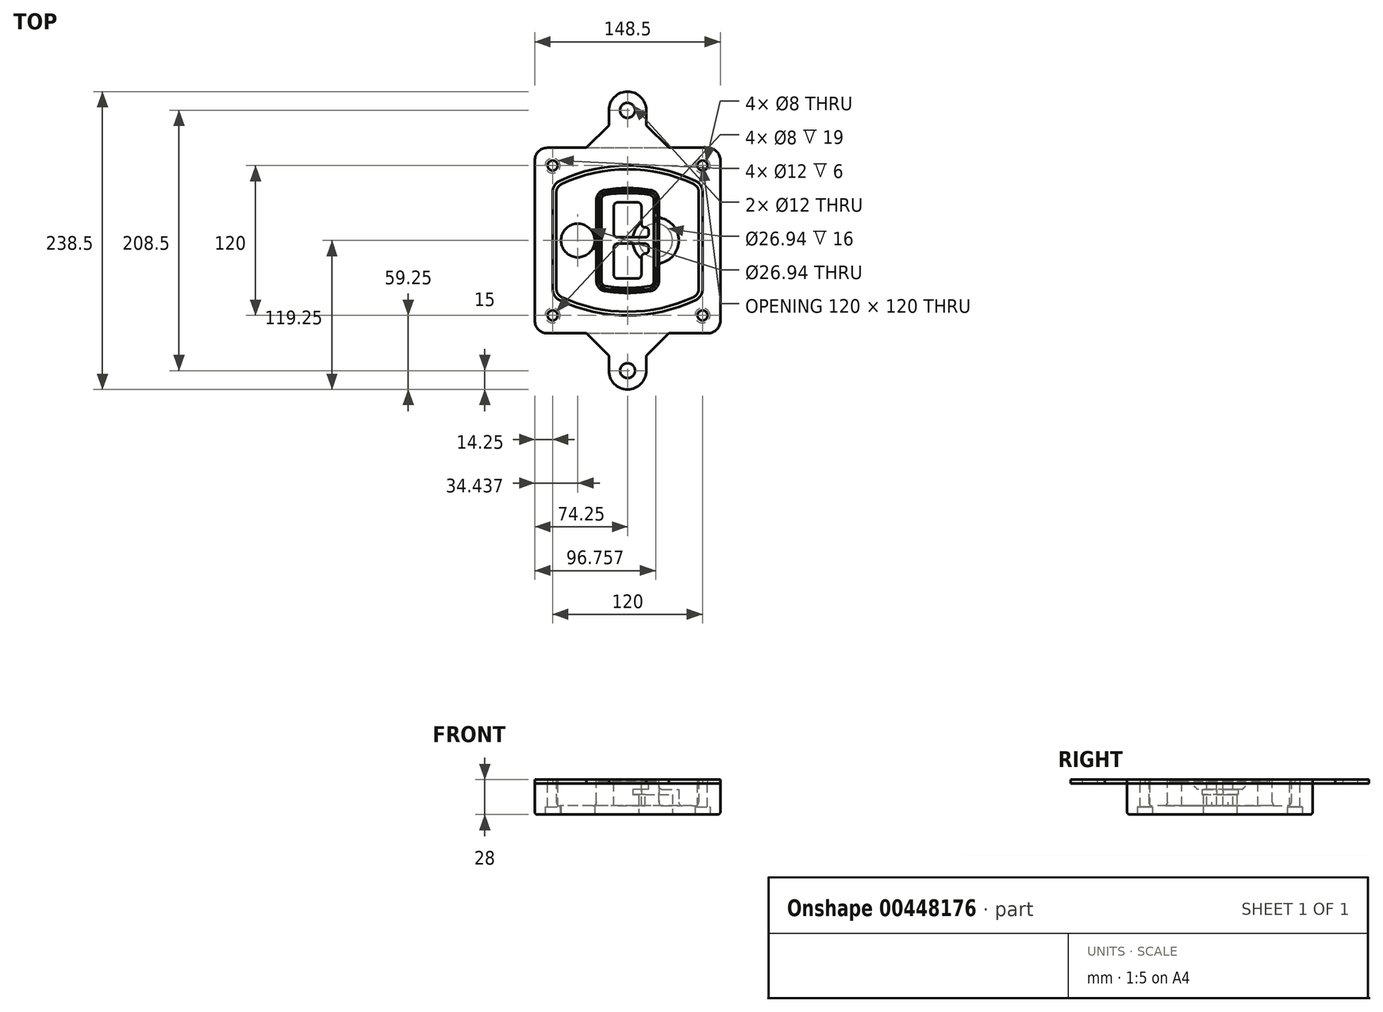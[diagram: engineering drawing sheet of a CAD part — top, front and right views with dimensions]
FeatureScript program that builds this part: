
annotation { "Feature Type Name" : "Feature", "Feature Type Description" : "" }
export const myFeature = defineFeature(function(context is Context, id is Id, definition is map)
    precondition{}
    {
        {
            var Q0;
            Q0=qCreatedBy(makeId("Top.planeOp"),FACE);
            var sketch = newSketch(context, id + "F0", { "sketchPlane" : qUnion([Q0])});
            skPoint(sketch, "E0.rect.middle", {"position": v(0, 0) * mm});
            skLineSegment(sketch, "E1.bottom", {"start": v(-64.25, -74.25) * mm, "end": v(64.25, -74.25) * mm});
            skLineSegment(sketch, "E1.top", {"start": v(-64.25, 74.25) * mm, "end": v(64.25, 74.25) * mm});
            skLineSegment(sketch, "E1.left", {"start": v(-74.25, -64.25) * mm, "end": v(-74.25, 64.25) * mm});
            skLineSegment(sketch, "E1.right", {"start": v(74.25, -64.25) * mm, "end": v(74.25, 64.25) * mm});
            skLineSegment(sketch, "E2", {"start": v(-74.25, 74.25) * mm, "end": v(74.25, -74.25) * mm, "construction": true});
            skLineSegment(sketch, "E3", {"start": v(74.25, 74.25) * mm, "end": v(-74.25, -74.25) * mm, "construction": true});
            skCircle(sketch, "E4", {"center": v(-60, 60) * mm, "radius": 4 * mm});
            skCircle(sketch, "E5", {"center": v(60, 60) * mm, "radius": 4 * mm});
            skCircle(sketch, "E6", {"center": v(60, -60) * mm, "radius": 4 * mm});
            skCircle(sketch, "E7", {"center": v(-60, -60) * mm, "radius": 4 * mm});
            skLineSegment(sketch, "E8", {"start": v(-60, 60) * mm, "end": v(60, 60) * mm, "construction": true});
            skLineSegment(sketch, "E9", {"start": v(60, 60) * mm, "end": v(60, -60) * mm, "construction": true});
            skLineSegment(sketch, "E10", {"start": v(60, -60) * mm, "end": v(-60, -60) * mm, "construction": true});
            skLineSegment(sketch, "E11", {"start": v(-60, -60) * mm, "end": v(-60, 60) * mm, "construction": true});
            skLineSegment(sketch, "E12", {"start": v(-60, 38.83) * mm, "end": v(-60, -38.83) * mm});
            skLineSegment(sketch, "E13", {"start": v(60, 38.83) * mm, "end": v(60, -38.83) * mm});
            skArc(sketch, "E14", {"start": v(54.26, 47.88) * mm, "mid": v(0, 60) * mm, "end": v(-54.26, 47.88) * mm});
            skArc(sketch, "E15", {"start": v(-54.26, -47.88) * mm, "mid": v(0, -60) * mm, "end": v(54.26, -47.88) * mm});
            skLineSegment(sketch, "E16", {"start": v(-60, 0) * mm, "end": v(60, 0) * mm, "construction": true});
            skPoint(sketch, "E17.visualSharp", {"position": v(-60, -45) * mm});
            skArc(sketch, "E17.filletArc", {"start": v(-60, -38.83) * mm, "mid": v(-58.44, -44.2) * mm, "end": v(-54.26, -47.88) * mm});
            skPoint(sketch, "E18.visualSharp", {"position": v(-60, 45) * mm});
            skArc(sketch, "E18.filletArc", {"start": v(-54.26, 47.88) * mm, "mid": v(-58.44, 44.2) * mm, "end": v(-60, 38.83) * mm});
            skPoint(sketch, "E19.visualSharp", {"position": v(60, 45) * mm});
            skArc(sketch, "E19.filletArc", {"start": v(60, 38.83) * mm, "mid": v(58.44, 44.2) * mm, "end": v(54.26, 47.88) * mm});
            skPoint(sketch, "E20.visualSharp", {"position": v(60, -45) * mm});
            skArc(sketch, "E20.filletArc", {"start": v(54.26, -47.88) * mm, "mid": v(58.44, -44.2) * mm, "end": v(60, -38.83) * mm});
            skPoint(sketch, "E21.visualSharp", {"position": v(-74.25, 74.25) * mm});
            skArc(sketch, "E21.filletArc", {"start": v(-64.25, 74.25) * mm, "mid": v(-71.32, 71.32) * mm, "end": v(-74.25, 64.25) * mm});
            skPoint(sketch, "E22.visualSharp", {"position": v(74.25, 74.25) * mm});
            skArc(sketch, "E22.filletArc", {"start": v(74.25, 64.25) * mm, "mid": v(71.32, 71.32) * mm, "end": v(64.25, 74.25) * mm});
            skPoint(sketch, "E23.visualSharp", {"position": v(74.25, -74.25) * mm});
            skArc(sketch, "E23.filletArc", {"start": v(64.25, -74.25) * mm, "mid": v(71.32, -71.32) * mm, "end": v(74.25, -64.25) * mm});
            skPoint(sketch, "E24.visualSharp", {"position": v(-74.25, -74.25) * mm});
            skArc(sketch, "E24.filletArc", {"start": v(-74.25, -64.25) * mm, "mid": v(-71.32, -71.32) * mm, "end": v(-64.25, -74.25) * mm});
            skArc(sketch, "E25.0", {"start": v(57, 38.83) * mm, "mid": v(55.9, 42.58) * mm, "end": v(52.98, 45.17) * mm});
            skLineSegment(sketch, "E25.1", {"start": v(57, 38.83) * mm, "end": v(57, -38.83) * mm});
            skArc(sketch, "E25.2", {"start": v(52.98, -45.17) * mm, "mid": v(55.9, -42.58) * mm, "end": v(57, -38.83) * mm});
            skArc(sketch, "E25.3", {"start": v(-52.98, -45.17) * mm, "mid": v(0, -57) * mm, "end": v(52.98, -45.17) * mm});
            skArc(sketch, "E25.4", {"start": v(-57, -38.83) * mm, "mid": v(-55.9, -42.58) * mm, "end": v(-52.98, -45.17) * mm});
            skArc(sketch, "E25.5", {"start": v(52.98, 45.17) * mm, "mid": v(0, 57) * mm, "end": v(-52.98, 45.17) * mm});
            skLineSegment(sketch, "E25.6", {"start": v(-57, 38.83) * mm, "end": v(-57, -38.83) * mm});
            skArc(sketch, "E25.7", {"start": v(-52.98, 45.17) * mm, "mid": v(-55.9, 42.58) * mm, "end": v(-57, 38.83) * mm});
            skArc(sketch, "E26.0", {"start": v(-55.96, 51.5) * mm, "mid": v(-61.82, 46.33) * mm, "end": v(-64, 38.83) * mm});
            skArc(sketch, "E26.1", {"start": v(55.96, 51.5) * mm, "mid": v(0, 64) * mm, "end": v(-55.96, 51.5) * mm});
            skArc(sketch, "E26.2", {"start": v(64, 38.83) * mm, "mid": v(61.82, 46.33) * mm, "end": v(55.96, 51.5) * mm});
            skLineSegment(sketch, "E26.3", {"start": v(64, 38.83) * mm, "end": v(64, -38.83) * mm});
            skArc(sketch, "E26.4", {"start": v(55.96, -51.5) * mm, "mid": v(61.82, -46.33) * mm, "end": v(64, -38.83) * mm});
            skLineSegment(sketch, "E26.5", {"start": v(-64, 38.83) * mm, "end": v(-64, -38.83) * mm});
            skArc(sketch, "E26.6", {"start": v(-55.96, -51.5) * mm, "mid": v(0, -64) * mm, "end": v(55.96, -51.5) * mm});
            skArc(sketch, "E26.7", {"start": v(-64, -38.83) * mm, "mid": v(-61.82, -46.33) * mm, "end": v(-55.96, -51.5) * mm});
            skSolve(sketch);
        }
        {
            var Q0;
            Q0=makeQuery(id+"F0.imprint","IMPRINT",FACE,{"disambiguationData":[TD([[makeQuery(id+"F0.imprint","IMPRINT",EDGE,{"derivedFrom":sQuery(id+"F0.wireOp",EDGE,"E1.bottom")}),1.0]])]});
            var Q1;
            Q1=makeQuery(id+"F0.imprint","IMPRINT",FACE,{"disambiguationData":[TD([[makeQuery(id+"F0.imprint","IMPRINT",EDGE,{"derivedFrom":sQuery(id+"F0.wireOp",EDGE,"E12")}),1.0]])]});
            var Q2;
            Q2=makeQuery(id+"F0.imprint","IMPRINT",FACE,{"disambiguationData":[TD([[makeQuery(id+"F0.imprint","IMPRINT",EDGE,{"derivedFrom":sQuery(id+"F0.wireOp",EDGE,"E25.0")}),1.0]])]});
            var Q3;
            Q3=makeQuery(id+"F0.imprint","IMPRINT",FACE,{"disambiguationData":[TD([[makeQuery(id+"F0.imprint","IMPRINT",EDGE,{"derivedFrom":sQuery(id+"F0.wireOp",EDGE,"E12")}),-1.0]])]});
            extrude(context, id + "F1", {"entities" : qUnion([Q0, Q1, Q2, Q3]), "oppositeDirection" : true, "depth" : 25 * mm});
        }
        {
            var Q0;
            Q0=makeQuery(id+"F0.imprint","IMPRINT",FACE,{"disambiguationData":[TD([[makeQuery(id+"F0.imprint","IMPRINT",EDGE,{"derivedFrom":sQuery(id+"F0.wireOp",EDGE,"E12")}),1.0]])]});
            extrude(context, id + "F2", {"entities" : qUnion([Q0]), "operationType" : NewBodyOperationType.ADD, "depth" : 3 * mm});
        }
        {
            var Q0;
            Q0=makeQuery(id+"F0.imprint","IMPRINT",FACE,{"disambiguationData":[TD([[makeQuery(id+"F0.imprint","IMPRINT",EDGE,{"derivedFrom":sQuery(id+"F0.wireOp",EDGE,"E25.0")}),1.0]])]});
            extrude(context, id + "F3", {"entities" : qUnion([Q0]), "operationType" : NewBodyOperationType.REMOVE, "oppositeDirection" : true, "depth" : 18 * mm});
        }
        {
            var Q0;
            Q0=makeQuery(id+"F2.opExtrude","CAP_FACE",FACE,{"disambiguationData":[OSD([sQuery(id+"F0.wireOp",EDGE,"E12"),sQuery(id+"F0.wireOp",EDGE,"E13"),sQuery(id+"F0.wireOp",EDGE,"E14"),sQuery(id+"F0.wireOp",EDGE,"E15"),sQuery(id+"F0.wireOp",EDGE,"E17.filletArc"),sQuery(id+"F0.wireOp",EDGE,"E18.filletArc"),sQuery(id+"F0.wireOp",EDGE,"E19.filletArc"),sQuery(id+"F0.wireOp",EDGE,"E20.filletArc"),sQuery(id+"F0.wireOp",EDGE,"E25.0"),sQuery(id+"F0.wireOp",EDGE,"E25.1"),sQuery(id+"F0.wireOp",EDGE,"E25.2"),sQuery(id+"F0.wireOp",EDGE,"E25.3"),sQuery(id+"F0.wireOp",EDGE,"E25.4"),sQuery(id+"F0.wireOp",EDGE,"E25.5"),sQuery(id+"F0.wireOp",EDGE,"E25.6"),sQuery(id+"F0.wireOp",EDGE,"E25.7")])],"isStart":false});
            var sketch = newSketch(context, id + "F4", { "sketchPlane" : qUnion([Q0])});
            skArc(sketch, "E27.0", {"start": v(-18.34, -40.45) * mm, "mid": v(0, -42) * mm, "end": v(18.34, -40.45) * mm});
            skArc(sketch, "E28.0", {"start": v(18.34, 40.45) * mm, "mid": v(0, 42) * mm, "end": v(-18.34, 40.45) * mm});
            skLineSegment(sketch, "E29", {"start": v(-25, 32.57) * mm, "end": v(-25, -32.57) * mm});
            skLineSegment(sketch, "E30", {"start": v(25, 32.57) * mm, "end": v(25, -32.57) * mm});
            skLineSegment(sketch, "E31", {"start": v(-25, 39.1) * mm, "end": v(25, 39.1) * mm, "construction": true});
            skLineSegment(sketch, "E32", {"start": v(-25, -39.1) * mm, "end": v(25, -39.1) * mm, "construction": true});
            skPoint(sketch, "E33.visualSharp", {"position": v(-25, 39.1) * mm});
            skArc(sketch, "E33.filletArc", {"start": v(-18.34, 40.45) * mm, "mid": v(-23.11, 37.73) * mm, "end": v(-25, 32.57) * mm});
            skPoint(sketch, "E34.visualSharp", {"position": v(25, 39.1) * mm});
            skArc(sketch, "E34.filletArc", {"start": v(25, 32.57) * mm, "mid": v(23.11, 37.73) * mm, "end": v(18.34, 40.45) * mm});
            skPoint(sketch, "E35.visualSharp", {"position": v(25, -39.1) * mm});
            skArc(sketch, "E35.filletArc", {"start": v(18.34, -40.45) * mm, "mid": v(23.11, -37.73) * mm, "end": v(25, -32.57) * mm});
            skPoint(sketch, "E36.visualSharp", {"position": v(-25, -39.1) * mm});
            skArc(sketch, "E36.filletArc", {"start": v(-25, -32.57) * mm, "mid": v(-23.11, -37.73) * mm, "end": v(-18.34, -40.45) * mm});
            skArc(sketch, "E37.0", {"start": v(52.98, 45.17) * mm, "mid": v(0, 57) * mm, "end": v(-52.98, 45.17) * mm});
            skArc(sketch, "E37.1", {"start": v(-52.98, 45.17) * mm, "mid": v(-55.9, 42.58) * mm, "end": v(-57, 38.83) * mm});
            skLineSegment(sketch, "E37.2", {"start": v(-57, 38.83) * mm, "end": v(-57, -38.83) * mm});
            skArc(sketch, "E37.3", {"start": v(-57, -38.83) * mm, "mid": v(-55.9, -42.58) * mm, "end": v(-52.98, -45.17) * mm});
            skArc(sketch, "E37.4", {"start": v(-52.98, -45.17) * mm, "mid": v(0, -57) * mm, "end": v(52.98, -45.17) * mm});
            skArc(sketch, "E37.5", {"start": v(52.98, -45.17) * mm, "mid": v(55.9, -42.58) * mm, "end": v(57, -38.83) * mm});
            skLineSegment(sketch, "E37.6", {"start": v(57, 38.83) * mm, "end": v(57, -38.83) * mm});
            skArc(sketch, "E37.7", {"start": v(57, 38.83) * mm, "mid": v(55.9, 42.58) * mm, "end": v(52.98, 45.17) * mm});
            skLineSegment(sketch, "E38.0", {"start": v(23, 32.57) * mm, "end": v(23, -32.57) * mm});
            skArc(sketch, "E38.1", {"start": v(18, -38.48) * mm, "mid": v(21.58, -36.44) * mm, "end": v(23, -32.57) * mm});
            skArc(sketch, "E38.2", {"start": v(-18, -38.48) * mm, "mid": v(0, -40) * mm, "end": v(18, -38.48) * mm});
            skArc(sketch, "E38.3", {"start": v(-23, -32.57) * mm, "mid": v(-21.58, -36.44) * mm, "end": v(-18, -38.48) * mm});
            skLineSegment(sketch, "E38.4", {"start": v(-23, 32.57) * mm, "end": v(-23, -32.57) * mm});
            skArc(sketch, "E38.5", {"start": v(23, 32.57) * mm, "mid": v(21.58, 36.44) * mm, "end": v(18, 38.48) * mm});
            skArc(sketch, "E38.6", {"start": v(-18, 38.48) * mm, "mid": v(-21.58, 36.44) * mm, "end": v(-23, 32.57) * mm});
            skArc(sketch, "E38.7", {"start": v(18, 38.48) * mm, "mid": v(0, 40) * mm, "end": v(-18, 38.48) * mm});
            skArc(sketch, "E39.0", {"start": v(21, 32.57) * mm, "mid": v(20.06, 35.15) * mm, "end": v(17.67, 36.5) * mm});
            skLineSegment(sketch, "E39.1", {"start": v(21, 32.57) * mm, "end": v(21, -32.57) * mm});
            skArc(sketch, "E39.2", {"start": v(17.67, -36.5) * mm, "mid": v(20.06, -35.15) * mm, "end": v(21, -32.57) * mm});
            skArc(sketch, "E39.3", {"start": v(-17.67, -36.5) * mm, "mid": v(0, -38) * mm, "end": v(17.67, -36.5) * mm});
            skArc(sketch, "E39.4", {"start": v(-21, -32.57) * mm, "mid": v(-20.06, -35.15) * mm, "end": v(-17.67, -36.5) * mm});
            skArc(sketch, "E39.5", {"start": v(17.67, 36.5) * mm, "mid": v(0, 38) * mm, "end": v(-17.67, 36.5) * mm});
            skLineSegment(sketch, "E39.6", {"start": v(-21, 32.57) * mm, "end": v(-21, -32.57) * mm});
            skArc(sketch, "E39.7", {"start": v(-17.67, 36.5) * mm, "mid": v(-20.06, 35.15) * mm, "end": v(-21, 32.57) * mm});
            skLineSegment(sketch, "E40", {"start": v(-25, 0) * mm, "end": v(25, 0) * mm, "construction": true});
            skLineSegment(sketch, "E41", {"start": v(-11, 5.5) * mm, "end": v(-11, 27.5) * mm});
            skLineSegment(sketch, "E42", {"start": v(-8, 30.5) * mm, "end": v(8, 30.5) * mm});
            skLineSegment(sketch, "E43", {"start": v(11, 27.5) * mm, "end": v(11, 13.5) * mm});
            skLineSegment(sketch, "E44", {"start": v(14, 10.5) * mm, "end": v(14, 10.5) * mm});
            skLineSegment(sketch, "E45", {"start": v(17, 7.5) * mm, "end": v(17, 5.5) * mm});
            skLineSegment(sketch, "E46", {"start": v(14, 2.5) * mm, "end": v(-8, 2.5) * mm});
            skPoint(sketch, "E47.visualSharp", {"position": v(-11, 30.5) * mm});
            skArc(sketch, "E47.filletArc", {"start": v(-8, 30.5) * mm, "mid": v(-10.12, 29.62) * mm, "end": v(-11, 27.5) * mm});
            skPoint(sketch, "E48.visualSharp", {"position": v(11, 30.5) * mm});
            skArc(sketch, "E48.filletArc", {"start": v(11, 27.5) * mm, "mid": v(10.12, 29.62) * mm, "end": v(8, 30.5) * mm});
            skPoint(sketch, "E49.visualSharp", {"position": v(11, 10.5) * mm});
            skArc(sketch, "E49.filletArc", {"start": v(11, 13.5) * mm, "mid": v(11.88, 11.38) * mm, "end": v(14, 10.5) * mm});
            skPoint(sketch, "E50.visualSharp", {"position": v(17, 10.5) * mm});
            skArc(sketch, "E50.filletArc", {"start": v(17, 7.5) * mm, "mid": v(16.12, 9.62) * mm, "end": v(14, 10.5) * mm});
            skPoint(sketch, "E51.visualSharp", {"position": v(17, 2.5) * mm});
            skArc(sketch, "E51.filletArc", {"start": v(14, 2.5) * mm, "mid": v(16.12, 3.38) * mm, "end": v(17, 5.5) * mm});
            skPoint(sketch, "E52.visualSharp", {"position": v(-11, 2.5) * mm});
            skArc(sketch, "E52.filletArc", {"start": v(-11, 5.5) * mm, "mid": v(-10.12, 3.38) * mm, "end": v(-8, 2.5) * mm});
            skLineSegment(sketch, "E53.0.MirrorCS", {"start": v(14, -2.5) * mm, "end": v(-8, -2.5) * mm});
            skArc(sketch, "E54.0.MirrorCS", {"start": v(-11, -5.5) * mm, "mid": v(-10.12, -3.38) * mm, "end": v(-8, -2.5) * mm});
            skLineSegment(sketch, "E55.0.MirrorCS", {"start": v(-11, -5.5) * mm, "end": v(-11, -27.5) * mm});
            skArc(sketch, "E56.0.MirrorCS", {"start": v(-8, -30.5) * mm, "mid": v(-10.12, -29.62) * mm, "end": v(-11, -27.5) * mm});
            skLineSegment(sketch, "E57.0.MirrorCS", {"start": v(-8, -30.5) * mm, "end": v(8, -30.5) * mm});
            skArc(sketch, "E58.0.MirrorCS", {"start": v(11, -27.5) * mm, "mid": v(10.12, -29.62) * mm, "end": v(8, -30.5) * mm});
            skLineSegment(sketch, "E59.0.MirrorCS", {"start": v(11, -27.5) * mm, "end": v(11, -13.5) * mm});
            skArc(sketch, "E60.0.MirrorCS", {"start": v(11, -13.5) * mm, "mid": v(11.88, -11.38) * mm, "end": v(14, -10.5) * mm});
            skArc(sketch, "E61.0.MirrorCS", {"start": v(17, -7.5) * mm, "mid": v(16.12, -9.62) * mm, "end": v(14, -10.5) * mm});
            skLineSegment(sketch, "E62.0.MirrorCS", {"start": v(17, -7.5) * mm, "end": v(17, -5.5) * mm});
            skArc(sketch, "E63.0.MirrorCS", {"start": v(14, -2.5) * mm, "mid": v(16.12, -3.38) * mm, "end": v(17, -5.5) * mm});
            skSolve(sketch);
        }
        {
            var Q0;
            Q0=makeQuery(id+"F4.imprint","IMPRINT",FACE,{"disambiguationData":[TD([[makeQuery(id+"F4.imprint","IMPRINT",EDGE,{"derivedFrom":sQuery(id+"F4.wireOp",EDGE,"E27.0")}),1.0]])]});
            var Q1;
            Q1=makeQuery(id+"F4.imprint","IMPRINT",FACE,{"disambiguationData":[TD([[makeQuery(id+"F4.imprint","IMPRINT",EDGE,{"derivedFrom":sQuery(id+"F4.wireOp",EDGE,"E38.0")}),-1.0]])]});
            var Q2;
            Q2=makeQuery(id+"F4.imprint","IMPRINT",FACE,{"disambiguationData":[TD([[makeQuery(id+"F4.imprint","IMPRINT",EDGE,{"derivedFrom":sQuery(id+"F4.wireOp",EDGE,"E39.0")}),1.0]])]});
            extrude(context, id + "F5", {"entities" : qUnion([Q0, Q1, Q2]), "operationType" : NewBodyOperationType.ADD, "endBound" : BoundingType.UP_TO_NEXT, "oppositeDirection" : true, "depth" : 25 * mm});
        }
        {
            var Q0;
            Q0=makeQuery(id+"F4.imprint","IMPRINT",FACE,{"disambiguationData":[TD([[makeQuery(id+"F4.imprint","IMPRINT",EDGE,{"derivedFrom":sQuery(id+"F4.wireOp",EDGE,"E38.0")}),-1.0]])]});
            extrude(context, id + "F6", {"entities" : qUnion([Q0]), "operationType" : NewBodyOperationType.REMOVE, "oppositeDirection" : true, "depth" : 2 * mm});
        }
        {
            var Q0;
            Q0=makeQuery(id+"F1.opExtrude","CAP_FACE",FACE,{"disambiguationData":[OSD([sQuery(id+"F0.wireOp",EDGE,"E1.bottom"),sQuery(id+"F0.wireOp",EDGE,"E1.top"),sQuery(id+"F0.wireOp",EDGE,"E1.left"),sQuery(id+"F0.wireOp",EDGE,"E1.right"),sQuery(id+"F0.wireOp",EDGE,"E4"),sQuery(id+"F0.wireOp",EDGE,"E5"),sQuery(id+"F0.wireOp",EDGE,"E6"),sQuery(id+"F0.wireOp",EDGE,"E7"),sQuery(id+"F0.wireOp",EDGE,"E21.filletArc"),sQuery(id+"F0.wireOp",EDGE,"E22.filletArc"),sQuery(id+"F0.wireOp",EDGE,"E23.filletArc"),sQuery(id+"F0.wireOp",EDGE,"E24.filletArc")])],"isStart":false});
            var sketch = newSketch(context, id + "F7", { "sketchPlane" : qUnion([Q0])});
            skCircle(sketch, "E64", {"center": v(22.5, 0) * mm, "radius": 13.47 * mm});
            skCircle(sketch, "E65", {"center": v(-39.81, 0) * mm, "radius": 13.47 * mm});
            skLineSegment(sketch, "E66", {"start": v(74.25, 0) * mm, "end": v(-74.25, 0) * mm});
            skCircle(sketch, "E67", {"center": v(22.5, 0) * mm, "radius": 18.47 * mm});
            skCircle(sketch, "E68", {"center": v(60, -60) * mm, "radius": 6 * mm});
            skCircle(sketch, "E69", {"center": v(-60, -60) * mm, "radius": 6 * mm});
            skCircle(sketch, "E70", {"center": v(-60, 60) * mm, "radius": 6 * mm});
            skCircle(sketch, "E71", {"center": v(60, 60) * mm, "radius": 6 * mm});
            skSolve(sketch);
        }
        {
            var Q0;
            {var subQ1=sQuery(id+"F7.wireOp",EDGE,"E66");var subQ4=sQuery(id+"F7.wireOp",EDGE,"E64");var subQ6=makeQuery(id+"F7.imprint","INTERSECT",VERTEX,{"disambiguationData":[OD(0.0)],"derivedFrom":[subQ4,subQ1]});Q0=makeQuery(id+"F7.imprint","IMPRINT",FACE,{"disambiguationData":[TD([[makeQuery(id+"F7.imprint","IMPRINT",EDGE,{"disambiguationData":[TD([[subQ6,-1.0]])],"derivedFrom":subQ4}),-1.0]])]});}
            var Q1;
            {var subQ0=sQuery(id+"F7.wireOp",EDGE,"E66");var subQ1=sQuery(id+"F7.wireOp",EDGE,"E64");var subQ3=makeQuery(id+"F7.imprint","INTERSECT",VERTEX,{"disambiguationData":[OD(0.0)],"derivedFrom":[subQ1,subQ0]});Q1=makeQuery(id+"F7.imprint","IMPRINT",FACE,{"disambiguationData":[TD([[makeQuery(id+"F7.imprint","IMPRINT",EDGE,{"disambiguationData":[TD([[subQ3,-1.0]])],"derivedFrom":subQ1}),1.0]])]});}
            var Q2;
            {var subQ0=sQuery(id+"F7.wireOp",EDGE,"E66");var subQ1=sQuery(id+"F7.wireOp",EDGE,"E64");var subQ3=makeQuery(id+"F7.imprint","INTERSECT",VERTEX,{"disambiguationData":[OD(0.0)],"derivedFrom":[subQ1,subQ0]});Q2=makeQuery(id+"F7.imprint","IMPRINT",FACE,{"disambiguationData":[TD([[makeQuery(id+"F7.imprint","IMPRINT",EDGE,{"disambiguationData":[TD([[subQ3,1.0]])],"derivedFrom":subQ1}),1.0]])]});}
            var Q3;
            {var subQ1=sQuery(id+"F7.wireOp",EDGE,"E66");var subQ4=sQuery(id+"F7.wireOp",EDGE,"E64");var subQ6=makeQuery(id+"F7.imprint","INTERSECT",VERTEX,{"disambiguationData":[OD(0.0)],"derivedFrom":[subQ4,subQ1]});Q3=makeQuery(id+"F7.imprint","IMPRINT",FACE,{"disambiguationData":[TD([[makeQuery(id+"F7.imprint","IMPRINT",EDGE,{"disambiguationData":[TD([[subQ6,1.0]])],"derivedFrom":subQ4}),-1.0]])]});}
            extrude(context, id + "F8", {"entities" : qUnion([Q0, Q1, Q2, Q3]), "operationType" : NewBodyOperationType.ADD, "oppositeDirection" : true, "depth" : 20 * mm});
        }
        {
            var Q0;
            {var subQ0=sQuery(id+"F7.wireOp",EDGE,"E66");var subQ1=sQuery(id+"F7.wireOp",EDGE,"E64");var subQ3=makeQuery(id+"F7.imprint","INTERSECT",VERTEX,{"disambiguationData":[OD(0.0)],"derivedFrom":[subQ1,subQ0]});Q0=makeQuery(id+"F7.imprint","IMPRINT",FACE,{"disambiguationData":[TD([[makeQuery(id+"F7.imprint","IMPRINT",EDGE,{"disambiguationData":[TD([[subQ3,-1.0]])],"derivedFrom":subQ1}),1.0]])]});}
            var Q1;
            {var subQ0=sQuery(id+"F7.wireOp",EDGE,"E66");var subQ1=sQuery(id+"F7.wireOp",EDGE,"E64");var subQ3=makeQuery(id+"F7.imprint","INTERSECT",VERTEX,{"disambiguationData":[OD(0.0)],"derivedFrom":[subQ1,subQ0]});Q1=makeQuery(id+"F7.imprint","IMPRINT",FACE,{"disambiguationData":[TD([[makeQuery(id+"F7.imprint","IMPRINT",EDGE,{"disambiguationData":[TD([[subQ3,1.0]])],"derivedFrom":subQ1}),1.0]])]});}
            extrude(context, id + "F9", {"entities" : qUnion([Q0, Q1]), "operationType" : NewBodyOperationType.REMOVE, "oppositeDirection" : true, "depth" : 16 * mm});
        }
        {
            var Q0;
            {var subQ0=sQuery(id+"F7.wireOp",EDGE,"E66");var subQ1=sQuery(id+"F7.wireOp",EDGE,"E65");var subQ3=makeQuery(id+"F7.imprint","INTERSECT",VERTEX,{"disambiguationData":[OD(0.0)],"derivedFrom":[subQ1,subQ0]});Q0=makeQuery(id+"F7.imprint","IMPRINT",FACE,{"disambiguationData":[TD([[makeQuery(id+"F7.imprint","IMPRINT",EDGE,{"disambiguationData":[TD([[subQ3,-1.0]])],"derivedFrom":subQ1}),1.0]])]});}
            var Q1;
            {var subQ0=sQuery(id+"F7.wireOp",EDGE,"E66");var subQ1=sQuery(id+"F7.wireOp",EDGE,"E65");var subQ3=makeQuery(id+"F7.imprint","INTERSECT",VERTEX,{"disambiguationData":[OD(0.0)],"derivedFrom":[subQ1,subQ0]});Q1=makeQuery(id+"F7.imprint","IMPRINT",FACE,{"disambiguationData":[TD([[makeQuery(id+"F7.imprint","IMPRINT",EDGE,{"disambiguationData":[TD([[subQ3,1.0]])],"derivedFrom":subQ1}),1.0]])]});}
            extrude(context, id + "F10", {"entities" : qUnion([Q0, Q1]), "operationType" : NewBodyOperationType.REMOVE, "oppositeDirection" : true, "depth" : 25 * mm});
        }
        {
            var Q0;
            Q0=makeQuery(id+"F7.imprint","IMPRINT",FACE,{"disambiguationData":[TD([[makeQuery(id+"F7.imprint","IMPRINT",EDGE,{"derivedFrom":sQuery(id+"F7.wireOp",EDGE,"E68")}),1.0]])]});
            var Q1;
            Q1=makeQuery(id+"F7.imprint","IMPRINT",FACE,{"disambiguationData":[TD([[makeQuery(id+"F7.imprint","IMPRINT",EDGE,{"derivedFrom":makeQuery(id+"F1.opExtrude","CAP_EDGE",EDGE,{"disambiguationData":[OSD([sQuery(id+"F0.wireOp",EDGE,"E5")])],"isStart":false})}),-1.0]])]});
            var Q2;
            Q2=makeQuery(id+"F7.imprint","IMPRINT",FACE,{"disambiguationData":[TD([[makeQuery(id+"F7.imprint","IMPRINT",EDGE,{"derivedFrom":sQuery(id+"F7.wireOp",EDGE,"E69")}),1.0]])]});
            var Q3;
            Q3=makeQuery(id+"F7.imprint","IMPRINT",FACE,{"disambiguationData":[TD([[makeQuery(id+"F7.imprint","IMPRINT",EDGE,{"derivedFrom":makeQuery(id+"F1.opExtrude","CAP_EDGE",EDGE,{"disambiguationData":[OSD([sQuery(id+"F0.wireOp",EDGE,"E4")])],"isStart":false})}),-1.0]])]});
            var Q4;
            Q4=makeQuery(id+"F7.imprint","IMPRINT",FACE,{"disambiguationData":[TD([[makeQuery(id+"F7.imprint","IMPRINT",EDGE,{"derivedFrom":sQuery(id+"F7.wireOp",EDGE,"E70")}),1.0]])]});
            var Q5;
            Q5=makeQuery(id+"F7.imprint","IMPRINT",FACE,{"disambiguationData":[TD([[makeQuery(id+"F7.imprint","IMPRINT",EDGE,{"derivedFrom":makeQuery(id+"F1.opExtrude","CAP_EDGE",EDGE,{"disambiguationData":[OSD([sQuery(id+"F0.wireOp",EDGE,"E7")])],"isStart":false})}),-1.0]])]});
            var Q6;
            Q6=makeQuery(id+"F7.imprint","IMPRINT",FACE,{"disambiguationData":[TD([[makeQuery(id+"F7.imprint","IMPRINT",EDGE,{"derivedFrom":sQuery(id+"F7.wireOp",EDGE,"E71")}),1.0]])]});
            var Q7;
            Q7=makeQuery(id+"F7.imprint","IMPRINT",FACE,{"disambiguationData":[TD([[makeQuery(id+"F7.imprint","IMPRINT",EDGE,{"derivedFrom":makeQuery(id+"F1.opExtrude","CAP_EDGE",EDGE,{"disambiguationData":[OSD([sQuery(id+"F0.wireOp",EDGE,"E6")])],"isStart":false})}),-1.0]])]});
            extrude(context, id + "F11", {"entities" : qUnion([Q0, Q1, Q2, Q3, Q4, Q5, Q6, Q7]), "operationType" : NewBodyOperationType.REMOVE, "oppositeDirection" : true, "depth" : 6 * mm});
        }
        {
            var Q0;
            Q0=makeQuery(id+"F9.boolean.opBoolean","COPY",FACE,{"derivedFrom":makeQuery(id+"F9.opExtrude","CAP_FACE",FACE,{"disambiguationData":[OSD([sQuery(id+"F7.wireOp",EDGE,"E64")])],"isStart":false})});
            var sketch = newSketch(context, id + "F12", { "sketchPlane" : qUnion([Q0])});
            skArc(sketch, "E72.0", {"start": v(11, 14.45) * mm, "mid": v(6.45, 9.13) * mm, "end": v(4.2, 2.5) * mm});
            skArc(sketch, "E72.1", {"start": v(4.2, -2.5) * mm, "mid": v(6.45, -9.13) * mm, "end": v(11, -14.45) * mm});
            skLineSegment(sketch, "E73", {"start": v(4.2, -2.5) * mm, "end": v(14, -2.5) * mm});
            skLineSegment(sketch, "E74.0", {"start": v(14, 2.5) * mm, "end": v(4.2, 2.5) * mm});
            skArc(sketch, "E74.1", {"start": v(14, 2.5) * mm, "mid": v(16.12, 3.38) * mm, "end": v(17, 5.5) * mm});
            skLineSegment(sketch, "E74.2", {"start": v(17, 7.5) * mm, "end": v(17, 5.5) * mm});
            skArc(sketch, "E74.3", {"start": v(17, 7.5) * mm, "mid": v(16.12, 9.62) * mm, "end": v(14, 10.5) * mm});
            skArc(sketch, "E74.4", {"start": v(11, 13.5) * mm, "mid": v(11.88, 11.38) * mm, "end": v(14, 10.5) * mm});
            skLineSegment(sketch, "E74.5", {"start": v(11, 14.45) * mm, "end": v(11, 13.5) * mm});
            skLineSegment(sketch, "E74.7", {"start": v(14, -2.5) * mm, "end": v(4.2, -2.5) * mm});
            skArc(sketch, "E74.8", {"start": v(14, -2.5) * mm, "mid": v(16.12, -3.38) * mm, "end": v(17, -5.5) * mm});
            skLineSegment(sketch, "E74.9", {"start": v(17, -7.5) * mm, "end": v(17, -5.5) * mm});
            skArc(sketch, "E74.10", {"start": v(17, -7.5) * mm, "mid": v(16.12, -9.62) * mm, "end": v(14, -10.5) * mm});
            skArc(sketch, "E74.11", {"start": v(11, -13.5) * mm, "mid": v(11.88, -11.38) * mm, "end": v(14, -10.5) * mm});
            skLineSegment(sketch, "E74.12", {"start": v(11, -14.45) * mm, "end": v(11, -13.5) * mm});
            skPoint(sketch, "E75.orphan", {"position": v(11, -27.5) * mm});
            skPoint(sketch, "E76.orphan", {"position": v(-8, -2.5) * mm});
            skPoint(sketch, "E77.orphan", {"position": v(-8, 2.5) * mm});
            skPoint(sketch, "E78.orphan", {"position": v(11, 27.5) * mm});
            skSolve(sketch);
        }
        {
            var Q0;
            {var subQ7=sQuery(id+"F12.wireOp",EDGE,"E72.0");var subQ14=sQuery(id+"F12.wireOp",EDGE,"E72.1");var subQ16=sQuery(id+"F12.wireOp",EDGE,"E74.1");var subQ18=sQuery(id+"F12.wireOp",EDGE,"E74.8");Q0=qUnion([makeQuery(id+"F12.imprint","IMPRINT",FACE,{"disambiguationData":[TD([[makeQuery(id+"F12.imprint","IMPRINT",EDGE,{"derivedFrom":subQ7}),1.0]])]}),makeQuery(id+"F12.imprint","IMPRINT",FACE,{"disambiguationData":[TD([[makeQuery(id+"F12.imprint","IMPRINT",EDGE,{"derivedFrom":subQ14}),1.0]])]}),makeQuery(id+"F12.imprint","IMPRINT",FACE,{"disambiguationData":[TD([[makeQuery(id+"F12.imprint","IMPRINT",EDGE,{"derivedFrom":subQ16}),1.0]])]}),makeQuery(id+"F12.imprint","IMPRINT",FACE,{"disambiguationData":[TD([[makeQuery(id+"F12.imprint","IMPRINT",EDGE,{"derivedFrom":subQ18}),-1.0]])]})]);}
            var Q1;
            Q1=makeQuery(id+"F5.boolean.opBoolean","SPLIT",FACE,{"disambiguationData":[TD([makeQuery(id+"F5.opExtrude","SWEPT_FACE",FACE,{"disambiguationData":[OSD([sQuery(id+"F4.wireOp",EDGE,"E41")])]})])],"derivedFrom":makeQuery(id+"F3.boolean.opBoolean","COPY",FACE,{"derivedFrom":makeQuery(id+"F3.opExtrude","CAP_FACE",FACE,{"disambiguationData":[OSD([sQuery(id+"F0.wireOp",EDGE,"E25.0"),sQuery(id+"F0.wireOp",EDGE,"E25.1"),sQuery(id+"F0.wireOp",EDGE,"E25.2"),sQuery(id+"F0.wireOp",EDGE,"E25.3"),sQuery(id+"F0.wireOp",EDGE,"E25.4"),sQuery(id+"F0.wireOp",EDGE,"E25.5"),sQuery(id+"F0.wireOp",EDGE,"E25.6"),sQuery(id+"F0.wireOp",EDGE,"E25.7")])],"isStart":false})})});
            extrude(context, id + "F13", {"entities" : qUnion([Q0]), "operationType" : NewBodyOperationType.REMOVE, "endBound" : BoundingType.UP_TO_SURFACE, "endBoundEntityFace" : qUnion([Q1]), "depth" : 25 * mm});
        }
        {
            var Q0;
            Q0=makeQuery(id+"F3.boolean.opBoolean","COPY",EDGE,{"derivedFrom":makeQuery(id+"F3.opExtrude","CAP_EDGE",EDGE,{"disambiguationData":[OSD([sQuery(id+"F0.wireOp",EDGE,"E25.6")])],"isStart":false})});
            var Q1;
            Q1=makeQuery(id+"F8.boolean.opBoolean","INTERSECT",EDGE,{"derivedFrom":[makeQuery(id+"F5.opExtrude","SWEPT_FACE",FACE,{"disambiguationData":[OSD([sQuery(id+"F4.wireOp",EDGE,"E30")])]}),makeQuery(id+"F8.opExtrude","CAP_FACE",FACE,{"disambiguationData":[OSD([sQuery(id+"F7.wireOp",EDGE,"E67")])],"isStart":false})]});
            var Q2;
            Q2=makeQuery(id+"F8.boolean.opBoolean","INTERSECT",EDGE,{"disambiguationData":[OD(1.0)],"derivedFrom":[makeQuery(id+"F5.opExtrude","SWEPT_FACE",FACE,{"disambiguationData":[OSD([sQuery(id+"F4.wireOp",EDGE,"E30")])]}),makeQuery(id+"F8.opExtrude","SWEPT_FACE",FACE,{"disambiguationData":[OSD([sQuery(id+"F7.wireOp",EDGE,"E67")])]})]});
            var Q3;
            {var subQ0=sQuery(id+"F4.wireOp",EDGE,"E30");Q3=makeQuery(id+"F8.boolean.opBoolean","SPLIT",EDGE,{"disambiguationData":[TD([makeQuery(id+"F5.opExtrude","SWEPT_FACE",FACE,{"disambiguationData":[OSD([sQuery(id+"F4.wireOp",EDGE,"E35.filletArc")])]})])],"derivedFrom":makeQuery(id+"F5.opExtrude","CAP_EDGE",EDGE,{"disambiguationData":[OSD([subQ0])],"isStart":false})});}
            var Q4;
            {var subQ0=sQuery(id+"F0.wireOp",EDGE,"E25.7");var subQ1=sQuery(id+"F0.wireOp",EDGE,"E25.1");var subQ2=sQuery(id+"F0.wireOp",EDGE,"E25.6");var subQ3=sQuery(id+"F0.wireOp",EDGE,"E25.5");var subQ4=sQuery(id+"F0.wireOp",EDGE,"E25.4");var subQ5=sQuery(id+"F0.wireOp",EDGE,"E25.0");var subQ6=sQuery(id+"F0.wireOp",EDGE,"E25.2");var subQ7=sQuery(id+"F0.wireOp",EDGE,"E25.3");Q4=makeQuery(id+"F8.boolean.opBoolean","INTERSECT",EDGE,{"derivedFrom":[makeQuery(id+"F5.boolean.opBoolean","SPLIT",FACE,{"disambiguationData":[TD([makeQuery(id+"F2.opExtrude","SWEPT_FACE",FACE,{"disambiguationData":[OSD([subQ5])]})])],"derivedFrom":makeQuery(id+"F3.boolean.opBoolean","COPY",FACE,{"derivedFrom":makeQuery(id+"F3.opExtrude","CAP_FACE",FACE,{"disambiguationData":[OSD([subQ5,subQ1,subQ6,subQ7,subQ4,subQ3,subQ2,subQ0])],"isStart":false})})}),makeQuery(id+"F8.opExtrude","SWEPT_FACE",FACE,{"disambiguationData":[OSD([sQuery(id+"F7.wireOp",EDGE,"E67")])]})]});}
            var Q5;
            Q5=makeQuery(id+"F8.boolean.opBoolean","INTERSECT",EDGE,{"disambiguationData":[OD(0.0)],"derivedFrom":[makeQuery(id+"F5.opExtrude","SWEPT_FACE",FACE,{"disambiguationData":[OSD([sQuery(id+"F4.wireOp",EDGE,"E30")])]}),makeQuery(id+"F8.opExtrude","SWEPT_FACE",FACE,{"disambiguationData":[OSD([sQuery(id+"F7.wireOp",EDGE,"E67")])]})]});
            fillet(context, id + "F14", {"entities" : qUnion([Q0, Q1, Q2, Q3, Q4, Q5]), "radius" : 3 * mm, "tangentPropagation" : true, "allowEdgeOverflow" : false});
        }
        {
            var Q0;
            Q0=makeQuery(id+"F1.opExtrude","CAP_EDGE",EDGE,{"disambiguationData":[OSD([sQuery(id+"F0.wireOp",EDGE,"E1.bottom")])],"isStart":false});
            fillet(context, id + "F15", {"entities" : qUnion([Q0]), "radius" : 2 * mm, "tangentPropagation" : true, "allowEdgeOverflow" : false});
        }
        {
            var Q0;
            {var subQ0=sQuery(id+"F0.wireOp",EDGE,"E21.filletArc");var subQ1=sQuery(id+"F0.wireOp",EDGE,"E7");var subQ2=sQuery(id+"F0.wireOp",EDGE,"E6");var subQ3=sQuery(id+"F0.wireOp",EDGE,"E5");var subQ4=sQuery(id+"F0.wireOp",EDGE,"E4");var subQ5=sQuery(id+"F0.wireOp",EDGE,"E22.filletArc");var subQ6=sQuery(id+"F0.wireOp",EDGE,"E1.bottom");var subQ7=sQuery(id+"F0.wireOp",EDGE,"E1.right");var subQ8=sQuery(id+"F0.wireOp",EDGE,"E1.top");var subQ9=sQuery(id+"F0.wireOp",EDGE,"E1.left");var subQ10=sQuery(id+"F0.wireOp",EDGE,"E23.filletArc");var subQ11=sQuery(id+"F0.wireOp",EDGE,"E24.filletArc");Q0=makeQuery(id+"F2.boolean.opBoolean","SPLIT",FACE,{"disambiguationData":[TD([makeQuery(id+"F1.opExtrude","SWEPT_FACE",FACE,{"disambiguationData":[OSD([subQ6])]})])],"derivedFrom":makeQuery(id+"F1.opExtrude","CAP_FACE",FACE,{"disambiguationData":[OSD([subQ6,subQ8,subQ9,subQ7,subQ4,subQ3,subQ2,subQ1,subQ0,subQ5,subQ10,subQ11])],"isStart":true})});}
            var sketch = newSketch(context, id + "F16", { "sketchPlane" : qUnion([Q0])});
            skLineSegment(sketch, "E79", {"start": v(0, 74.25) * mm, "end": v(0, 104.25) * mm, "construction": true});
            skCircle(sketch, "E80", {"center": v(0, 104.25) * mm, "radius": 6 * mm});
            skLineSegment(sketch, "E81", {"start": v(-15, 104.25) * mm, "end": v(-15, 92.25) * mm});
            skLineSegment(sketch, "E82", {"start": v(-15, 92.25) * mm, "end": v(-33, 74.25) * mm});
            skLineSegment(sketch, "E83", {"start": v(15, 104.25) * mm, "end": v(15, 92.25) * mm});
            skLineSegment(sketch, "E84", {"start": v(15, 92.25) * mm, "end": v(33, 74.25) * mm});
            skArc(sketch, "E85", {"start": v(15, 104.25) * mm, "mid": v(0, 119.25) * mm, "end": v(-15, 104.25) * mm});
            skLineSegment(sketch, "E86", {"start": v(-74.25, 0) * mm, "end": v(74.25, 0) * mm, "construction": true});
            skLineSegment(sketch, "E87.MirrorCS", {"start": v(15, -104.25) * mm, "end": v(15, -92.25) * mm});
            skLineSegment(sketch, "E88.MirrorCS", {"start": v(-15, -104.25) * mm, "end": v(-15, -92.25) * mm});
            skLineSegment(sketch, "E89.MirrorCS", {"start": v(0, -74.25) * mm, "end": v(0, -104.25) * mm, "construction": true});
            skArc(sketch, "E90.MirrorCS", {"start": v(15, -104.25) * mm, "mid": v(0, -119.25) * mm, "end": v(-15, -104.25) * mm});
            skLineSegment(sketch, "E91.MirrorCS", {"start": v(-15, -92.25) * mm, "end": v(-33, -74.25) * mm});
            skCircle(sketch, "E92.MirrorC", {"center": v(0, -104.25) * mm, "radius": 6 * mm});
            skLineSegment(sketch, "E93.MirrorCS", {"start": v(15, -92.25) * mm, "end": v(33, -74.25) * mm});
            skSolve(sketch);
        }
        {
            var Q0;
            Q0=makeQuery(id+"F16.imprint","IMPRINT",FACE,{"disambiguationData":[TD([[makeQuery(id+"F16.imprint","IMPRINT",EDGE,{"derivedFrom":sQuery(id+"F16.wireOp",EDGE,"E87.MirrorCS")}),1.0]])]});
            var Q1;
            Q1=makeQuery(id+"F16.imprint","IMPRINT",FACE,{"disambiguationData":[TD([[makeQuery(id+"F16.imprint","IMPRINT",EDGE,{"derivedFrom":makeQuery(id+"F1.opExtrude","CAP_EDGE",EDGE,{"disambiguationData":[OSD([sQuery(id+"F0.wireOp",EDGE,"E1.left")])],"isStart":true})}),-1.0]])]});
            var Q2;
            Q2=makeQuery(id+"F16.imprint","IMPRINT",FACE,{"disambiguationData":[TD([[makeQuery(id+"F16.imprint","IMPRINT",EDGE,{"derivedFrom":sQuery(id+"F16.wireOp",EDGE,"E80")}),-1.0]])]});
            var Q3;
            Q3=makeQuery(id+"F2.opExtrude","CAP_FACE",FACE,{"disambiguationData":[OSD([sQuery(id+"F0.wireOp",EDGE,"E12"),sQuery(id+"F0.wireOp",EDGE,"E13"),sQuery(id+"F0.wireOp",EDGE,"E14"),sQuery(id+"F0.wireOp",EDGE,"E15"),sQuery(id+"F0.wireOp",EDGE,"E17.filletArc"),sQuery(id+"F0.wireOp",EDGE,"E18.filletArc"),sQuery(id+"F0.wireOp",EDGE,"E19.filletArc"),sQuery(id+"F0.wireOp",EDGE,"E20.filletArc"),sQuery(id+"F0.wireOp",EDGE,"E25.0"),sQuery(id+"F0.wireOp",EDGE,"E25.1"),sQuery(id+"F0.wireOp",EDGE,"E25.2"),sQuery(id+"F0.wireOp",EDGE,"E25.3"),sQuery(id+"F0.wireOp",EDGE,"E25.4"),sQuery(id+"F0.wireOp",EDGE,"E25.5"),sQuery(id+"F0.wireOp",EDGE,"E25.6"),sQuery(id+"F0.wireOp",EDGE,"E25.7")])],"isStart":false});
            extrude(context, id + "F17", {"entities" : qUnion([Q0, Q1, Q2]), "endBound" : BoundingType.UP_TO_SURFACE, "depth" : 25 * mm, "endBoundEntityFace" : qUnion([Q3]), "offsetDistance" : 25 * mm});
        }
    });
